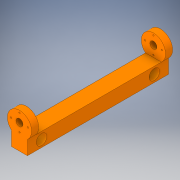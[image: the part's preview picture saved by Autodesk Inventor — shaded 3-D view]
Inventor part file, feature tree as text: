
AUTODESK INVENTOR PART (.ipt)
format: ipt  version: 2019 (Build 230136000, 136)  size: 166,912 bytes
history: native  units: in
note: dims shown in document units (in); Inventor stores cm internally (conversion verified against a paired STEP export)
features: extrude x3, sketch x3, plane x1, mirror x1
ambient origin geometry x8: Origin, YZ Plane, XZ Plane, XY Plane, X Axis, Y Axis, Z Axis, Center Point
bodies: Solid1 (feature_tree)
feature tree (8):
  extrude  "Extrusion1"  Depth=0.565in
  extrude  "Extrusion2"  Depth=0.5in
  sketch  "Sketch3"  dims[d5=0.375in d6=4.0in d7=5.0in d8=0.5in d9=0.5in d10=0.25in d11=0.25in d12=0.5in d13=0.0in d15=0.75in d16=0.0469in d17=0.0469in d18=0.0469in d19=0.0469in d20=0.3in d28=0.0in d29=0.43in d32=0.25in d33=0.3in d34=0.3in d35=0.3in d36=0.0in d37=0.3792in d38=0.0in d39=0.0in d40=0.0in d41=0.25in d42=0.0in]
  plane  "Work Plane1"
  extrude  "Extrusion4"  Depth=0.25in
  mirror  "Mirror1"
  sketch  "Sketch1"  dims[d0=5.0in d1=0.565in]
  sketch  "Sketch2"  dims[d2=0.5in d3=0.0in d4=0.375in]
